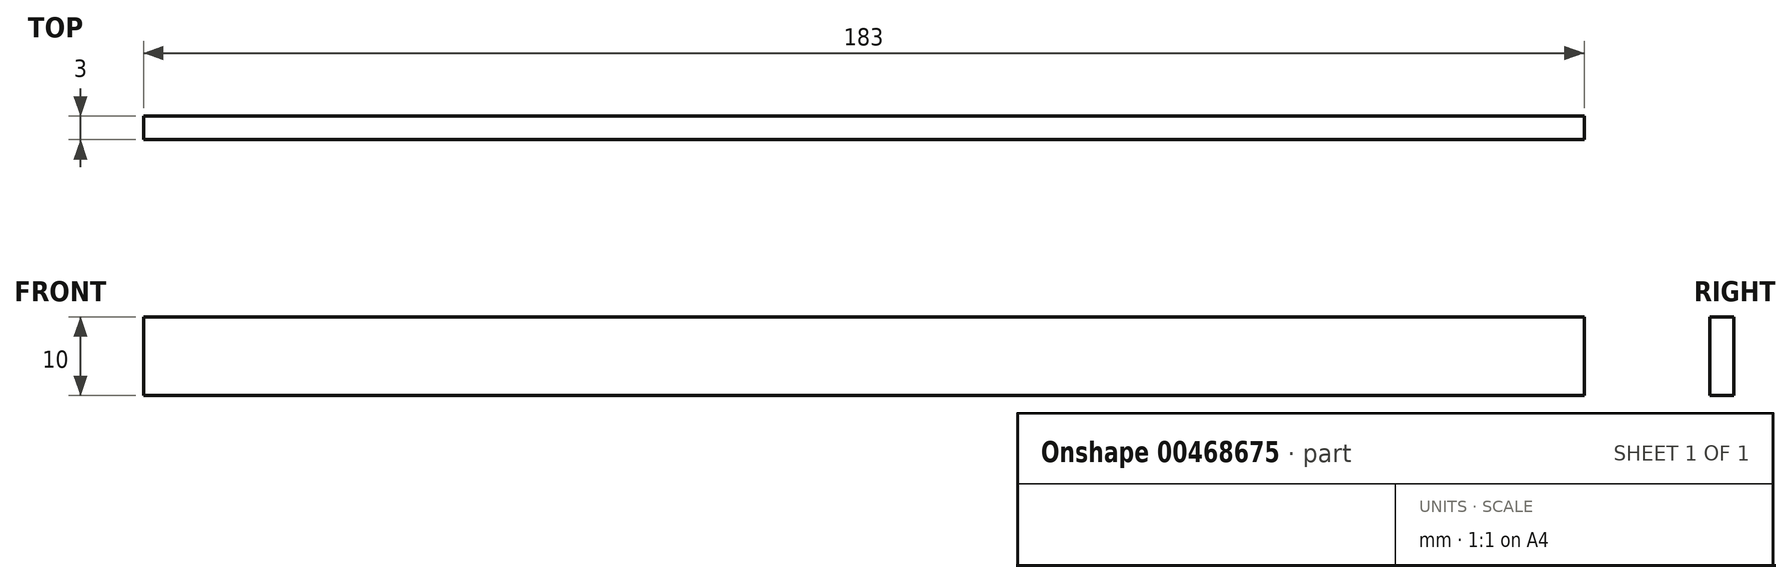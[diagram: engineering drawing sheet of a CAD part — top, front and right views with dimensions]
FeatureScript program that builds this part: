
annotation { "Feature Type Name" : "Feature", "Feature Type Description" : "" }
export const myFeature = defineFeature(function(context is Context, id is Id, definition is map)
    precondition{}
    {
        {
            var Q0;
            Q0=qCreatedBy(makeId("Front.planeOp"),FACE);
            var sketch = newSketch(context, id + "F0", { "sketchPlane" : qUnion([Q0])});
            skLineSegment(sketch, "E0.bottom", {"start": v(91.5, -5) * mm, "end": v(-91.5, -5) * mm});
            skLineSegment(sketch, "E0.top", {"start": v(91.5, 5) * mm, "end": v(-91.5, 5) * mm});
            skLineSegment(sketch, "E0.left", {"start": v(91.5, -5) * mm, "end": v(91.5, 5) * mm});
            skLineSegment(sketch, "E0.right", {"start": v(-91.5, -5) * mm, "end": v(-91.5, 5) * mm});
            skPoint(sketch, "E0.middle", {"position": v(0, 0) * mm});
            skSolve(sketch);
        }
        {
            var Q0;
            Q0=makeQuery(id+"F0.imprint","IMPRINT",FACE,{"disambiguationData":[TD([[makeQuery(id+"F0.imprint","IMPRINT",EDGE,{"derivedFrom":sQuery(id+"F0.wireOp",EDGE,"E0.bottom")}),-1.0]])]});
            extrude(context, id + "F1", {"entities" : qUnion([Q0]), "depth" : 3 * mm});
        }
    });
